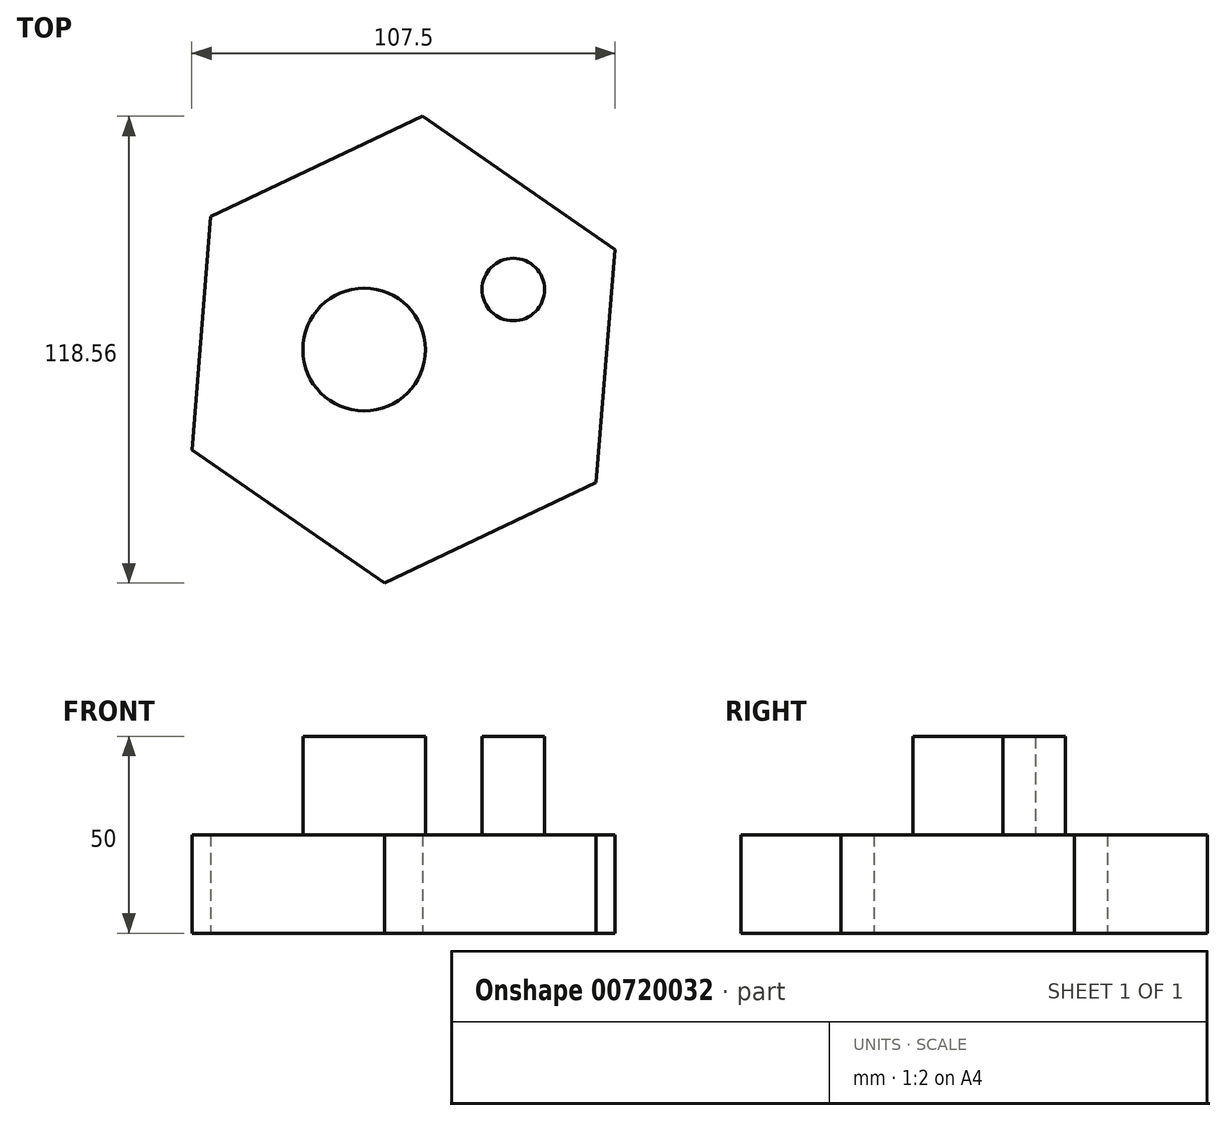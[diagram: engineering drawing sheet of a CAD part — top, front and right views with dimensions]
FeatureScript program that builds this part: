
annotation { "Feature Type Name" : "Feature", "Feature Type Description" : "" }
export const myFeature = defineFeature(function(context is Context, id is Id, definition is map)
    precondition{}
    {
        {
            var Q0;
            Q0=qCreatedBy(makeId("Top.planeOp"),FACE);
            var sketch = newSketch(context, id + "F0", { "sketchPlane" : qUnion([Q0])});
            skCircle(sketch, "E0.cCircle", {"center": v(0, 0) * mm, "radius": 51.5 * mm, "construction": true});
            skLineSegment(sketch, "E0.0", {"start": v(-48.93, 33.8) * mm, "end": v(4.81, 59.28) * mm});
            skLineSegment(sketch, "E0.1", {"start": v(4.81, 59.28) * mm, "end": v(53.75, 25.47) * mm});
            skLineSegment(sketch, "E0.2", {"start": v(53.75, 25.47) * mm, "end": v(48.93, -33.8) * mm});
            skLineSegment(sketch, "E0.3", {"start": v(48.93, -33.8) * mm, "end": v(-4.81, -59.28) * mm});
            skLineSegment(sketch, "E0.4", {"start": v(-4.81, -59.28) * mm, "end": v(-53.75, -25.47) * mm});
            skLineSegment(sketch, "E0.5", {"start": v(-53.75, -25.47) * mm, "end": v(-48.93, 33.8) * mm});
            skPoint(sketch, "E0.0.midPoint", {"position": v(-22.06, 46.55) * mm});
            skSolve(sketch);
        }
        {
            var Q0;
            Q0=makeQuery(id+"F0.imprint","IMPRINT",FACE,{"disambiguationData":[TD([[makeQuery(id+"F0.imprint","IMPRINT",EDGE,{"derivedFrom":sQuery(id+"F0.wireOp",EDGE,"E0.0")}),-1.0]])]});
            extrude(context, id + "F1", {"entities" : qUnion([Q0]), "depth" : 25 * mm, "offsetDistance" : 25 * mm});
        }
        {
            var Q0;
            Q0=makeQuery(id+"F1.opExtrude","CAP_FACE",FACE,{"disambiguationData":[OSD([sQuery(id+"F0.wireOp",EDGE,"E0.0"),sQuery(id+"F0.wireOp",EDGE,"E0.1"),sQuery(id+"F0.wireOp",EDGE,"E0.2"),sQuery(id+"F0.wireOp",EDGE,"E0.3"),sQuery(id+"F0.wireOp",EDGE,"E0.4"),sQuery(id+"F0.wireOp",EDGE,"E0.5")])],"isStart":false});
            var sketch = newSketch(context, id + "F2", { "sketchPlane" : qUnion([Q0])});
            skCircle(sketch, "E1", {"center": v(-9.97, 0) * mm, "radius": 15.58 * mm});
            skSolve(sketch);
        }
        {
            var Q0;
            Q0=makeQuery(id+"F2.imprint","IMPRINT",FACE,{"disambiguationData":[TD([[makeQuery(id+"F2.imprint","IMPRINT",EDGE,{"derivedFrom":sQuery(id+"F2.wireOp",EDGE,"E1")}),1.0]])]});
            extrude(context, id + "F3", {"entities" : qUnion([Q0]), "operationType" : NewBodyOperationType.ADD, "depth" : 25 * mm, "offsetDistance" : 25 * mm});
        }
        {
            var Q0;
            Q0=makeQuery(id+"F1.opExtrude","CAP_FACE",FACE,{"disambiguationData":[OSD([sQuery(id+"F0.wireOp",EDGE,"E0.0"),sQuery(id+"F0.wireOp",EDGE,"E0.1"),sQuery(id+"F0.wireOp",EDGE,"E0.2"),sQuery(id+"F0.wireOp",EDGE,"E0.3"),sQuery(id+"F0.wireOp",EDGE,"E0.4"),sQuery(id+"F0.wireOp",EDGE,"E0.5")])],"isStart":false});
            var sketch = newSketch(context, id + "F4", { "sketchPlane" : qUnion([Q0])});
            skCircle(sketch, "E2", {"center": v(27.92, 15.27) * mm, "radius": 7.95 * mm});
            skSolve(sketch);
        }
        {
            var Q0;
            Q0=makeQuery(id+"F4.imprint","IMPRINT",FACE,{"disambiguationData":[TD([[makeQuery(id+"F4.imprint","IMPRINT",EDGE,{"derivedFrom":sQuery(id+"F4.wireOp",EDGE,"E2")}),1.0]])]});
            extrude(context, id + "F5", {"entities" : qUnion([Q0]), "operationType" : NewBodyOperationType.ADD, "depth" : 25 * mm, "offsetDistance" : 25 * mm});
        }
    });
